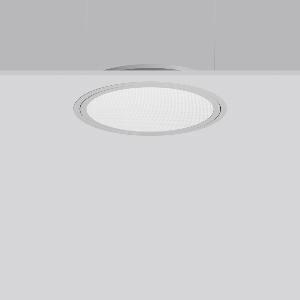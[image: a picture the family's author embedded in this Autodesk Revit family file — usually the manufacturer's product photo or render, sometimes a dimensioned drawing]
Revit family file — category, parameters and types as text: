
# Revit family: triona_round_e_312423_004_2_12_a4a3
name_source: partatom
category: Lighting Fixtures
units: mm (PartAtom-declared; Revit-internal decimal feet)

## family parameters
Cut with Voids When Loaded = No
Host = Face
Light Source = No
Part Type = Normal
Room Calculation Point = No
Round Connector Dimension = Use Diameter
Shared = No

## types (1)
- TuneableWhite 846 (1 x LED Modul 846, 2700 lm, 4600)
    Apparent Load = 29 VA
    CIE Flux Codes = 58 87 97 100 100
    Color Rendering = 80
    Color Temperature = 4600
    Default Elevation = 1800 mm
    Description = Series: TRIONA round
Decorative round LED recessed surface luminaire. Cover made of sheet steel, powder-coated. Frame made of aluminium, powder-coated. Recessed ring: aluminium extrusion profile, powder coated. Light emission through a diffuser in plastic, opal/prismatic. Lightguide and diffuser made of non-yellowing plastic (PMMA). Lateral light emission (RZB SIDELITE technology) for above-average homogeneous light distribution. Tunable white versions, dynamically adjustable from 2700 K to 6500 K. Suitable for installation in cavity ceilings. Tool-free mounting system thanks to the rocker arm mechanism (patent pending). Electronic ballast included. Very easy installation thanks to Plug+Play connection. Ideal for use as part of the Human Centric Lighting concept in connection with RZB light management systems. 
Colour: silver, matt (approx. RAL 9006)
Diameter: 505 mm
Height: 2 mm
Cut-out diameter: 482 mm
Recess height: 100 mm
Luminaire: recess height: 89 mm
Lamp: LED
Socket: without socket
Colour temperature: 2700K - 6500K
Colour rendering index (CRI): 80
System power: 29 W
Rated luminous flux: 2700 lm
Luminous efficiency: 93 lm/W
System power 2: 29 W
Rated luminous flux 2: 2550 lm
Luminous efficiency 2: 88 lm/W
System power 3: 30 W
Rated luminous flux 3: 2600 lm
Luminous efficiency 3: 87 lm/W
Control gear: Converter, dimmable, DALI
Protection class: I
Type of protection: IP 40
    Height = 0 mm  [stored 0 ft]
    Lamp = 1 x LED Modul 846
    Lamp Light Flux = 2700 lm
    Lamp count = 1
    Length = 505 mm
    Lifetime = 50000 h
    Luminous efficacy = 93 lm/W
    Manufacturer = RZB
    ModVariant = No
    Model = 312423.004.2.12
    Mounting Place = Ceiling
    Mounting Type = Recessed
    Number of Poles = 1
    OnlyDefault = Yes
    Power Factor = 1
    Product Name = TRIONA round E
    Product group = Recessed modular luminaires
    ProductGroupID = 406
    Protection Class = Protection class I
    Protection Degree = IP 20
    RLX_Detail_Level = 1
    RLX_Emergency_Light_Flux = 0 lm
    RLX_Emergency_Type = 0
    RLX_Emergency_Type_DB = No
    RlxData = <blob elided: 32517 chars, md5=5dfedaf3>
    Socket = socket
    Standby Power = 0 W
    System Light Flux = 2700 lm
    System Power = 29 W
    Type Comments = TuneableWhite 846
    Type Image = 312423.004.12.jpg
    URL = http://relux.com
    VarID = tuneablewhite_846
    Voltage = 230 V
    Voltage Range = 220-240 V
    Weight = 0.00 kg
    Width = 0 mm  [stored 0 ft]

note: [stored X ft] marks values corroborated as IEEE doubles in the binary element streams (Revit-internal decimal feet)

## geometry (parser evidence)
native form markers: Blend x4, Sweep x9
no freeform markers — native parametric forms only
